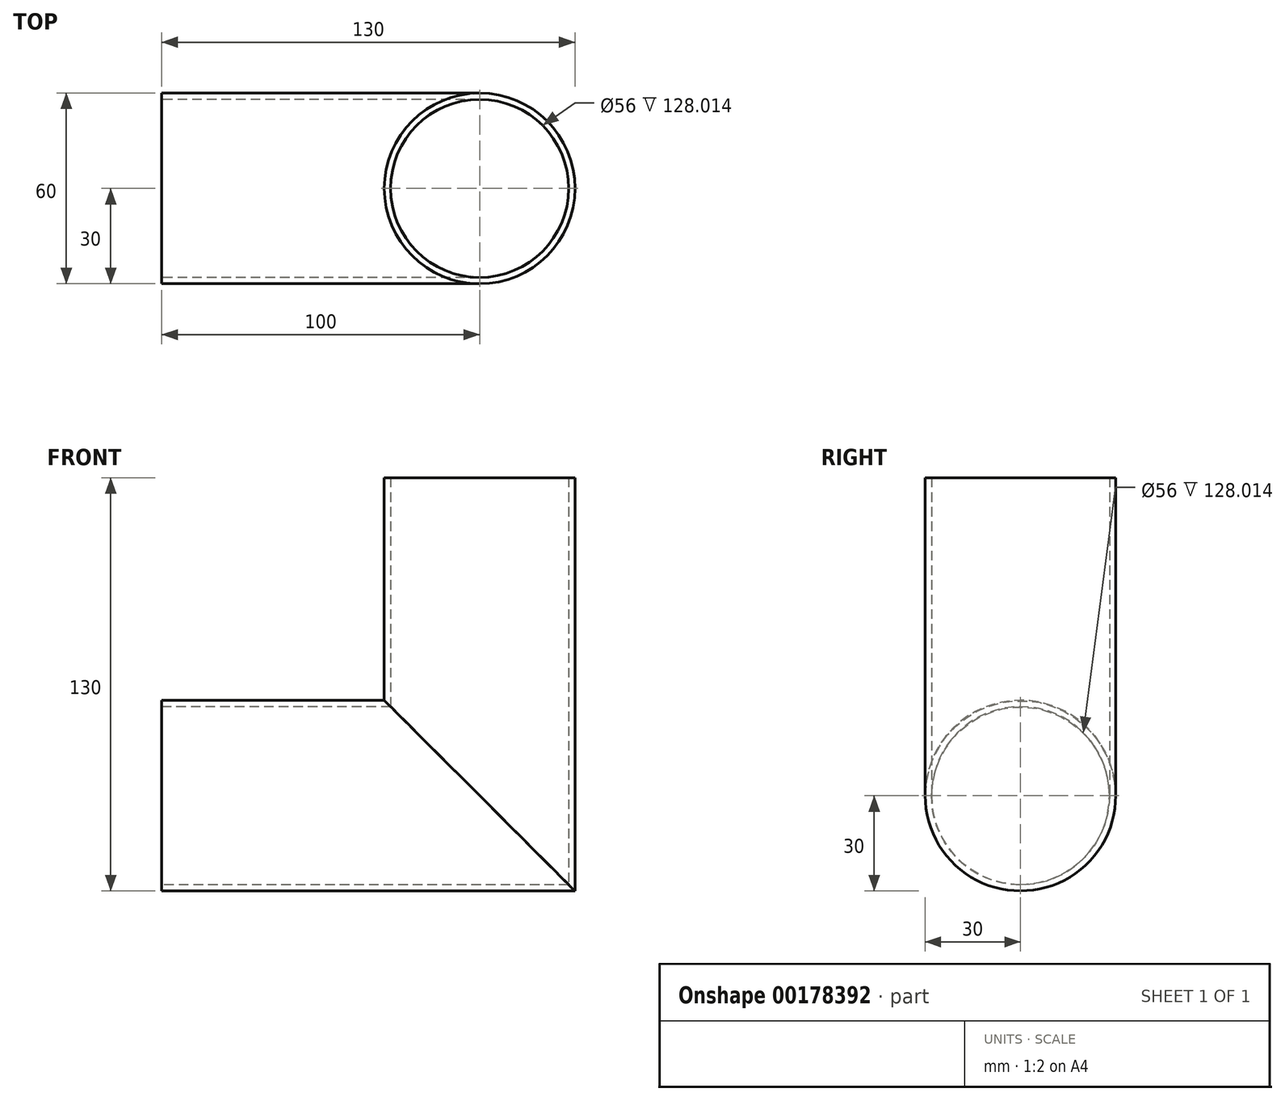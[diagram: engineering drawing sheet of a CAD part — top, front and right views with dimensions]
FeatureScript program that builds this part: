
annotation { "Feature Type Name" : "Feature", "Feature Type Description" : "" }
export const myFeature = defineFeature(function(context is Context, id is Id, definition is map)
    precondition{}
    {
        {
            var Q0;
            Q0=qCreatedBy(makeId("Front.planeOp"),FACE);
            var sketch = newSketch(context, id + "F0", { "sketchPlane" : qUnion([Q0])});
            skLineSegment(sketch, "E0", {"start": v(-100, 0) * mm, "end": v(0, 0) * mm});
            skLineSegment(sketch, "E1", {"start": v(0, 0) * mm, "end": v(0, 100) * mm});
            skSolve(sketch);
        }
        {
            var Q0;
            Q0=sQuery(id+"F0.wireOp",VERTEX,"E1.end");
            var Q1;
            Q1=qCreatedBy(makeId("Top.planeOp"),FACE);
            cPlane(context, id + "F1", {"entities" : qUnion([Q0, Q1]), "cplaneType" : CPlaneType.PLANE_POINT, "offset" : 25 * mm, "width" : 150 * mm, "height" : 150 * mm});
        }
        {
            var Q0;
            Q0=qCreatedBy(id+"F1.planeOp",FACE);
            var sketch = newSketch(context, id + "F2", { "sketchPlane" : qUnion([Q0])});
            skCircle(sketch, "E2", {"center": v(0, 0) * mm, "radius": 30 * mm});
            skCircle(sketch, "E3.0", {"center": v(0, 0) * mm, "radius": 28 * mm});
            skSolve(sketch);
        }
        {
            var Q0;
            Q0=makeQuery(id+"F2.imprint","IMPRINT",FACE,{"disambiguationData":[TD([[makeQuery(id+"F2.imprint","IMPRINT",EDGE,{"derivedFrom":sQuery(id+"F2.wireOp",EDGE,"E2")}),1.0]])]});
            var Q1;
            Q1=sQuery(id+"F0.wireOp",EDGE,"E1");
            var Q2;
            Q2=sQuery(id+"F0.wireOp",EDGE,"E0");
            sweep(context, id + "F3", {"profiles" : qUnion([Q0]), "path" : qUnion([Q1, Q2])});
        }
    });
